# Revit family: Clarus_beClear_R20
name_source: partatom
category: Furniture
units: mm (PartAtom-declared; Revit-internal decimal feet)

## family parameters
Cut with Voids When Loaded = No
Host = Face
Room Calculation Point = No
Shared = No

## types (2) — shared parameters
Core Thickness = 1/2"
Default Elevation = 0"
Depth = 21"
Description = be! Clear is an innovative, non-porous mobile glassboard that serves many
purposes. Whether you use it as a protective shield from today’s various health
threats, as a collaborative writing surface, or as a temporary space divider that
won’t impact the integrity of your open-concept offi ce design, you can keep
everyone healthy and at a safe distance without impeding the sightline from
one end of your space to the other. The optional cutout feature allows you to
safely take the temperature of incoming employees, customers or visitors, as
well as handoff important documents through an easily sanitized barrier while
safeguarding everyone. Thanks to the natural properties of glass, be! Clear is
safety and mobility rolled into one perfect solution.
Leg Length = 10 1/4"
Manufacturer = Clarus
Model = be! Clear
Modeled By = Commense Studio
Product URL = https://www.clarus.com
URL = https://www.clarus.com
Width = 40"

## per-type parameters (varying)
| type | Caster | Height | Leg Height |
| 40" X 21" Casters | Yes | 73" | 2 5/8" |
| 40" X 21" No Casters | No | 70 3/8" | 0" |

## geometry (parser evidence)
native form markers: Sweep x7
no freeform markers — native parametric forms only
